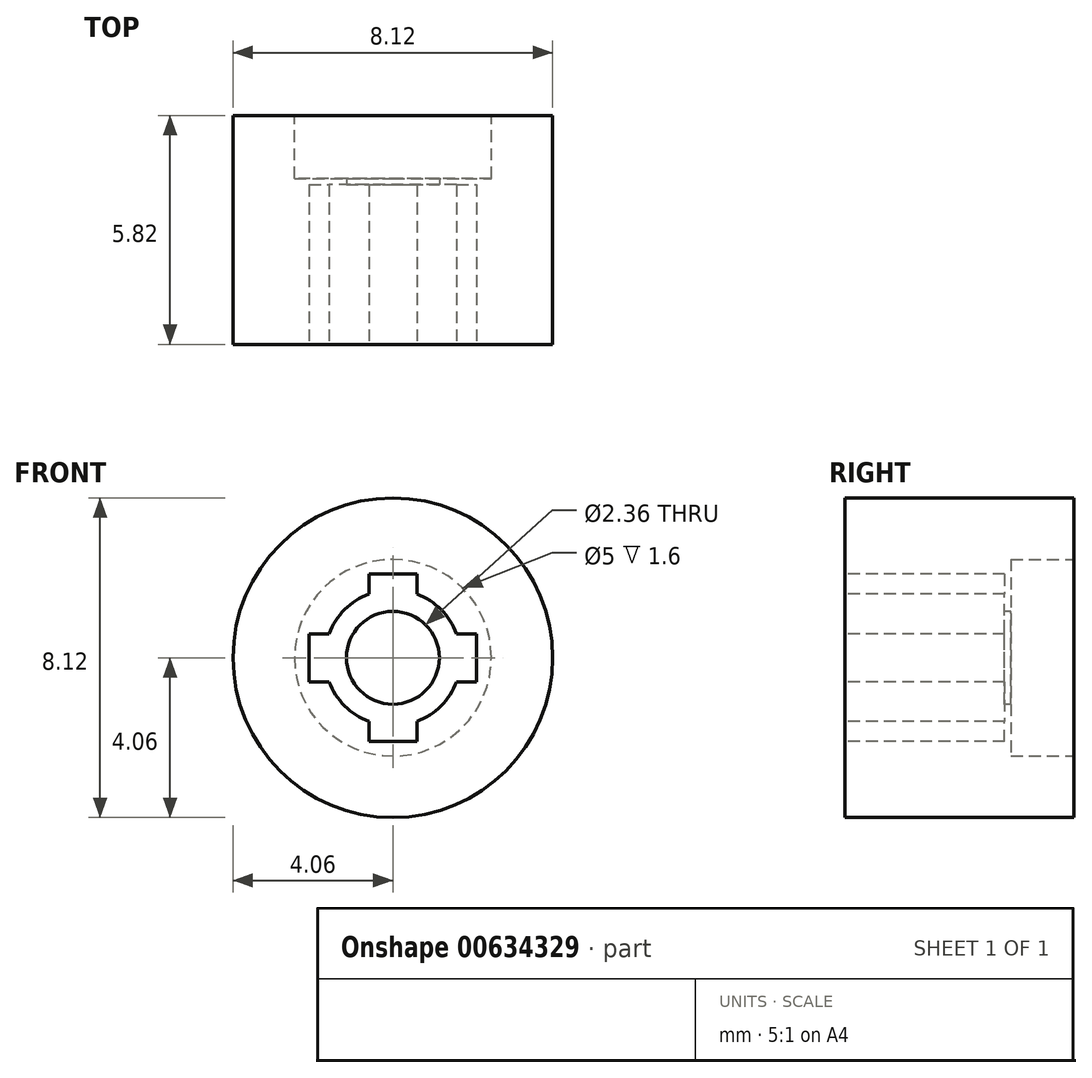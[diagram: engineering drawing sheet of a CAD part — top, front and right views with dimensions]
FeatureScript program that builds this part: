
annotation { "Feature Type Name" : "Feature", "Feature Type Description" : "" }
export const myFeature = defineFeature(function(context is Context, id is Id, definition is map)
    precondition{}
    {
        {
            var Q0;
            Q0=qCreatedBy(makeId("Front.planeOp"),FACE);
            var sketch = newSketch(context, id + "F0", { "sketchPlane" : qUnion([Q0])});
            skCircle(sketch, "E0", {"center": v(0, 0) * mm, "radius": 4.06 * mm});
            skSolve(sketch);
        }
        {
            var Q0;
            Q0=qSketchRegion(id+"F0",true);
            var Q1;
            Q1=qSketchRegion(id+"F2",true);
            extrude(context, id + "F1", {"entities" : qUnion([Q0, Q1]), "depth" : 5.82 * mm});
        }
        {
            var Q0;
            Q0=makeQuery(id+"F1.opExtrude","CAP_FACE",FACE,{"disambiguationData":[OSD([sQuery(id+"F0.wireOp",EDGE,"E0")])],"isStart":false});
            var sketch = newSketch(context, id + "F2", { "sketchPlane" : qUnion([Q0])});
            skCircle(sketch, "E1", {"center": v(0, 0) * mm, "radius": 1.73 * mm});
            skLineSegment(sketch, "E2", {"start": v(-0.61, 1.62) * mm, "end": v(-0.61, 2.13) * mm});
            skLineSegment(sketch, "E3", {"start": v(-0.61, 2.13) * mm, "end": v(0.61, 2.13) * mm});
            skLineSegment(sketch, "E4", {"start": v(0.61, 2.13) * mm, "end": v(0.61, 1.62) * mm});
            skLineSegment(sketch, "E5.1.0", {"start": v(-2.13, -0.61) * mm, "end": v(-2.13, 0.61) * mm});
            skLineSegment(sketch, "E5.1.1", {"start": v(-1.62, -0.61) * mm, "end": v(-2.13, -0.61) * mm});
            skLineSegment(sketch, "E5.1.2", {"start": v(-2.13, 0.61) * mm, "end": v(-1.62, 0.61) * mm});
            skLineSegment(sketch, "E5.2.0", {"start": v(0.6, -2.13) * mm, "end": v(-0.61, -2.13) * mm});
            skLineSegment(sketch, "E5.2.1", {"start": v(0.61, -1.62) * mm, "end": v(0.6, -2.13) * mm});
            skLineSegment(sketch, "E5.2.2", {"start": v(-0.61, -2.13) * mm, "end": v(-0.61, -1.62) * mm});
            skLineSegment(sketch, "E5.3.0", {"start": v(2.13, 0.6) * mm, "end": v(2.13, -0.61) * mm});
            skLineSegment(sketch, "E5.3.1", {"start": v(1.62, 0.6) * mm, "end": v(2.13, 0.6) * mm});
            skLineSegment(sketch, "E5.3.2", {"start": v(2.13, -0.61) * mm, "end": v(1.62, -0.61) * mm});
            skSolve(sketch);
        }
        {
            var Q0;
            Q0=qSketchRegion(id+"F2",true);
            extrude(context, id + "F3", {"entities" : qUnion([Q0]), "operationType" : NewBodyOperationType.REMOVE, "oppositeDirection" : true, "depth" : 4.06 * mm});
        }
        {
            var Q0;
            Q0=makeQuery(id+"F3.boolean.opBoolean","COPY",FACE,{"derivedFrom":makeQuery(id+"F3.opExtrude","CAP_FACE",FACE,{"disambiguationData":[OSD([sQuery(id+"F2.wireOp",EDGE,"E1"),sQuery(id+"F2.wireOp",EDGE,"E2"),sQuery(id+"F2.wireOp",EDGE,"E3"),sQuery(id+"F2.wireOp",EDGE,"E4"),sQuery(id+"F2.wireOp",EDGE,"E5.1.0"),sQuery(id+"F2.wireOp",EDGE,"E5.1.1"),sQuery(id+"F2.wireOp",EDGE,"E5.1.2"),sQuery(id+"F2.wireOp",EDGE,"E5.2.0"),sQuery(id+"F2.wireOp",EDGE,"E5.2.1"),sQuery(id+"F2.wireOp",EDGE,"E5.2.2"),sQuery(id+"F2.wireOp",EDGE,"E5.3.0"),sQuery(id+"F2.wireOp",EDGE,"E5.3.1"),sQuery(id+"F2.wireOp",EDGE,"E5.3.2")])],"isStart":false})});
            var sketch = newSketch(context, id + "F4", { "sketchPlane" : qUnion([Q0])});
            skCircle(sketch, "E6", {"center": v(0, 0) * mm, "radius": 1.18 * mm});
            skSolve(sketch);
        }
        {
            var Q0;
            Q0=qSketchRegion(id+"F4",true);
            extrude(context, id + "F5", {"entities" : qUnion([Q0]), "operationType" : NewBodyOperationType.REMOVE, "oppositeDirection" : true, "depth" : 25 * mm});
        }
        {
            var Q0;
            Q0=makeQuery(id+"F1.opExtrude","CAP_FACE",FACE,{"disambiguationData":[OSD([sQuery(id+"F0.wireOp",EDGE,"E0")])],"isStart":true});
            var sketch = newSketch(context, id + "F6", { "sketchPlane" : qUnion([Q0])});
            skCircle(sketch, "E7", {"center": v(0, 0) * mm, "radius": 2.5 * mm});
            skSolve(sketch);
        }
        {
            var Q0;
            Q0=makeQuery(id+"F6.imprint","IMPRINT",FACE,{"disambiguationData":[TD([[makeQuery(id+"F6.imprint","IMPRINT",EDGE,{"derivedFrom":sQuery(id+"F6.wireOp",EDGE,"E7")}),1.0]])]});
            extrude(context, id + "F7", {"entities" : qUnion([Q0]), "operationType" : NewBodyOperationType.REMOVE, "oppositeDirection" : true, "depth" : 1.6 * mm});
        }
    });
